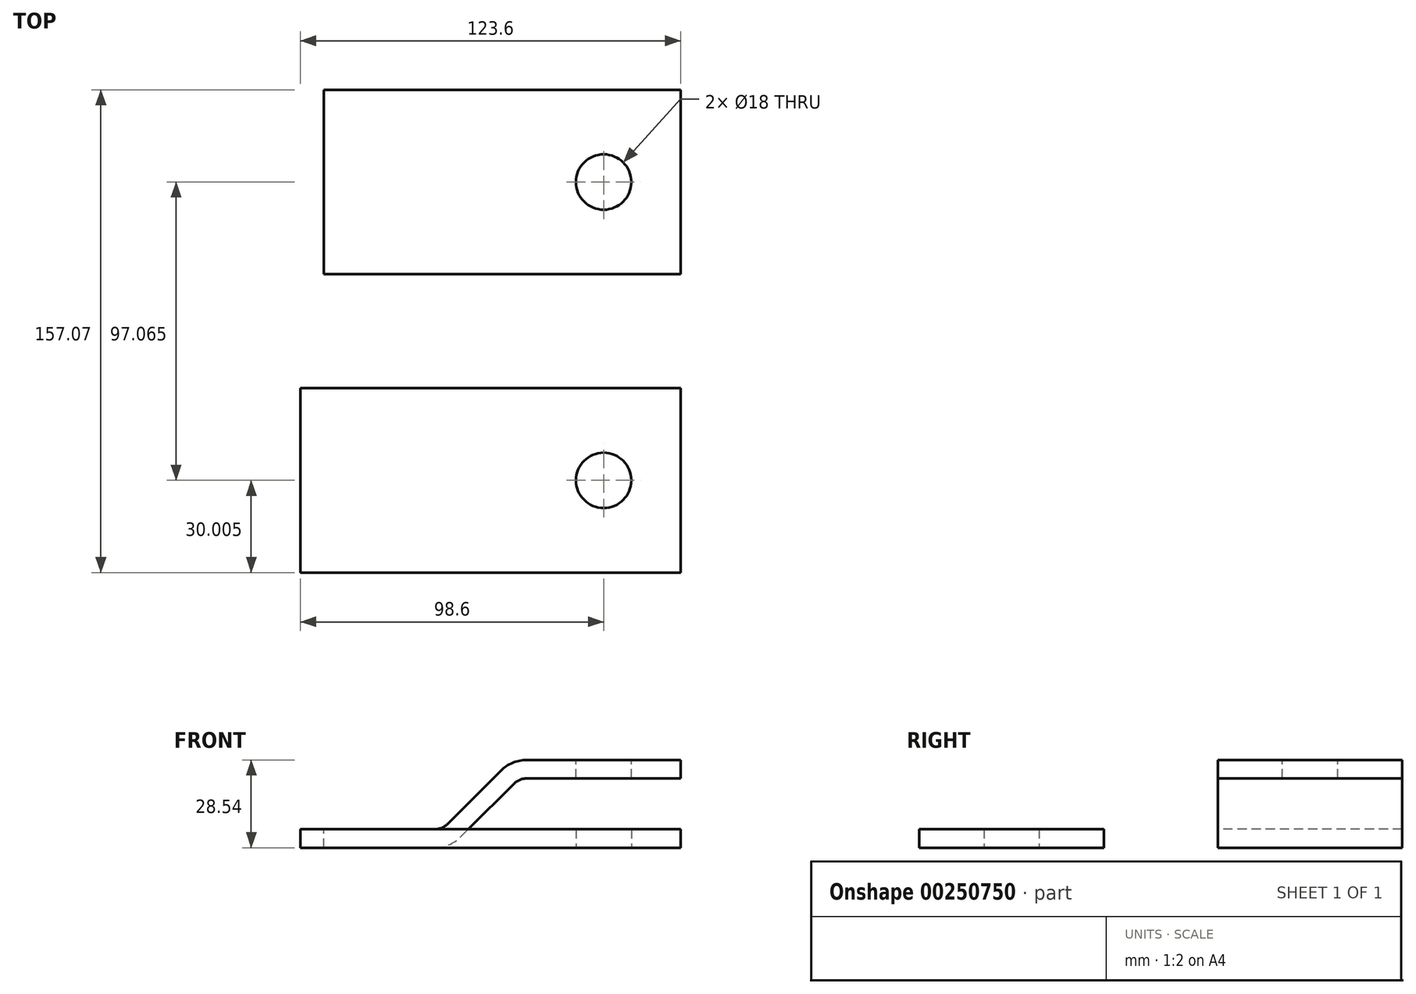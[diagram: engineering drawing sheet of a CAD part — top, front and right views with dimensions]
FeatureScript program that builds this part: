
annotation { "Feature Type Name" : "Feature", "Feature Type Description" : "" }
export const myFeature = defineFeature(function(context is Context, id is Id, definition is map)
    precondition{}
    {
        {
            var Q0;
            Q0=qCreatedBy(makeId("Front.planeOp"),FACE);
            var sketch = newSketch(context, id + "F0", { "sketchPlane" : qUnion([Q0])});
            skLineSegment(sketch, "E0.0", {"start": v(36, 0) * mm, "end": v(0, 0) * mm});
            skLineSegment(sketch, "E0.1", {"start": v(44.49, 3.51) * mm, "end": v(61.76, 20.79) * mm});
            skLineSegment(sketch, "E1", {"start": v(116, 22.54) * mm, "end": v(66, 22.54) * mm});
            skLineSegment(sketch, "E2.0", {"start": v(0, 43.5) * mm, "end": v(0, -37.5) * mm, "construction": true});
            skPoint(sketch, "E3.visualSharp", {"position": v(40.97, 0) * mm});
            skLineSegment(sketch, "E4", {"start": v(0, 0) * mm, "end": v(0, 6) * mm});
            skLineSegment(sketch, "E5", {"start": v(0, 6) * mm, "end": v(36, 6) * mm});
            skLineSegment(sketch, "E6", {"start": v(40.24, 7.76) * mm, "end": v(57.51, 25.03) * mm});
            skLineSegment(sketch, "E7", {"start": v(66, 28.54) * mm, "end": v(116, 28.54) * mm});
            skLineSegment(sketch, "E8", {"start": v(116, 28.54) * mm, "end": v(116, 22.54) * mm});
            skLineSegment(sketch, "E9", {"start": v(-94, 43.5) * mm, "end": v(-94, -37.5) * mm, "construction": true});
            skLineSegment(sketch, "E10", {"start": v(-6, 43.5) * mm, "end": v(-6, -37.5) * mm, "construction": true});
            skLineSegment(sketch, "E11", {"start": v(91, 43.5) * mm, "end": v(91, 0) * mm, "construction": true});
            skPoint(sketch, "E12.visualSharp", {"position": v(63.51, 22.54) * mm});
            skArc(sketch, "E12.filletArc", {"start": v(66, 22.54) * mm, "mid": v(63.7, 22.09) * mm, "end": v(61.76, 20.79) * mm});
            skPoint(sketch, "E13.visualSharp", {"position": v(38.49, 6) * mm});
            skArc(sketch, "E13.filletArc", {"start": v(36, 6) * mm, "mid": v(38.3, 6.46) * mm, "end": v(40.24, 7.76) * mm});
            skPoint(sketch, "E14.visualSharp", {"position": v(61.03, 28.54) * mm});
            skArc(sketch, "E14.filletArc", {"start": v(66, 28.54) * mm, "mid": v(61.4, 27.63) * mm, "end": v(57.51, 25.03) * mm});
            skArc(sketch, "E15.filletArc", {"start": v(36, 0) * mm, "mid": v(40.6, 0.91) * mm, "end": v(44.49, 3.51) * mm});
            skSolve(sketch);
        }
        {
            var Q0;
            Q0 = qSketchRegion(id + "F0", true);
            extrude(context, id + "F1", {"entities" : qUnion([Q0]), "oppositeDirection" : true, "depth" : 60 * mm});
        }
        {
            var Q0;
            Q0=makeQuery(id+"F1.opExtrude","SWEPT_FACE",FACE,{"disambiguationData":[OSD([sQuery(id+"F0.wireOp",EDGE,"E7")])]});
            var sketch = newSketch(context, id + "F2", { "sketchPlane" : qUnion([Q0])});
            skCircle(sketch, "E16", {"center": v(91, 30) * mm, "radius": 9 * mm});
            skLineSegment(sketch, "E17", {"start": v(-94, 60) * mm, "end": v(-94, 0) * mm, "construction": true});
            skLineSegment(sketch, "E18", {"start": v(-6, 60) * mm, "end": v(-6, 0) * mm, "construction": true});
            skLineSegment(sketch, "E19", {"start": v(0, 60) * mm, "end": v(0, 0) * mm, "construction": true});
            skSolve(sketch);
        }
        {
            var Q0;
            Q0 = qSketchRegion(id + "F2", true);
            extrude(context, id + "F3", {"entities" : qUnion([Q0]), "operationType" : NewBodyOperationType.REMOVE, "oppositeDirection" : true, "depth" : 25 * mm});
        }
        {
            var Q0;
            Q0=qCreatedBy(makeId("Top.planeOp"),FACE);
            var sketch = newSketch(context, id + "F4", { "sketchPlane" : qUnion([Q0])});
            skLineSegment(sketch, "E20.bottom", {"start": v(116, -37.07) * mm, "end": v(-7.6, -37.07) * mm});
            skLineSegment(sketch, "E20.top", {"start": v(116, -97.07) * mm, "end": v(-7.6, -97.07) * mm});
            skLineSegment(sketch, "E20.left", {"start": v(116, -37.07) * mm, "end": v(116, -97.07) * mm});
            skLineSegment(sketch, "E20.right", {"start": v(-7.6, -37.07) * mm, "end": v(-7.6, -97.07) * mm});
            skCircle(sketch, "E21", {"center": v(91, -67.07) * mm, "radius": 9 * mm});
            skLineSegment(sketch, "E22.0", {"start": v(116, 60) * mm, "end": v(116, 0) * mm, "construction": true});
            skSolve(sketch);
        }
        {
            var Q0;
            Q0 = qSketchRegion(id + "F4", true);
            extrude(context, id + "F5", {"entities" : qUnion([Q0]), "depth" : 6 * mm});
        }
    });
